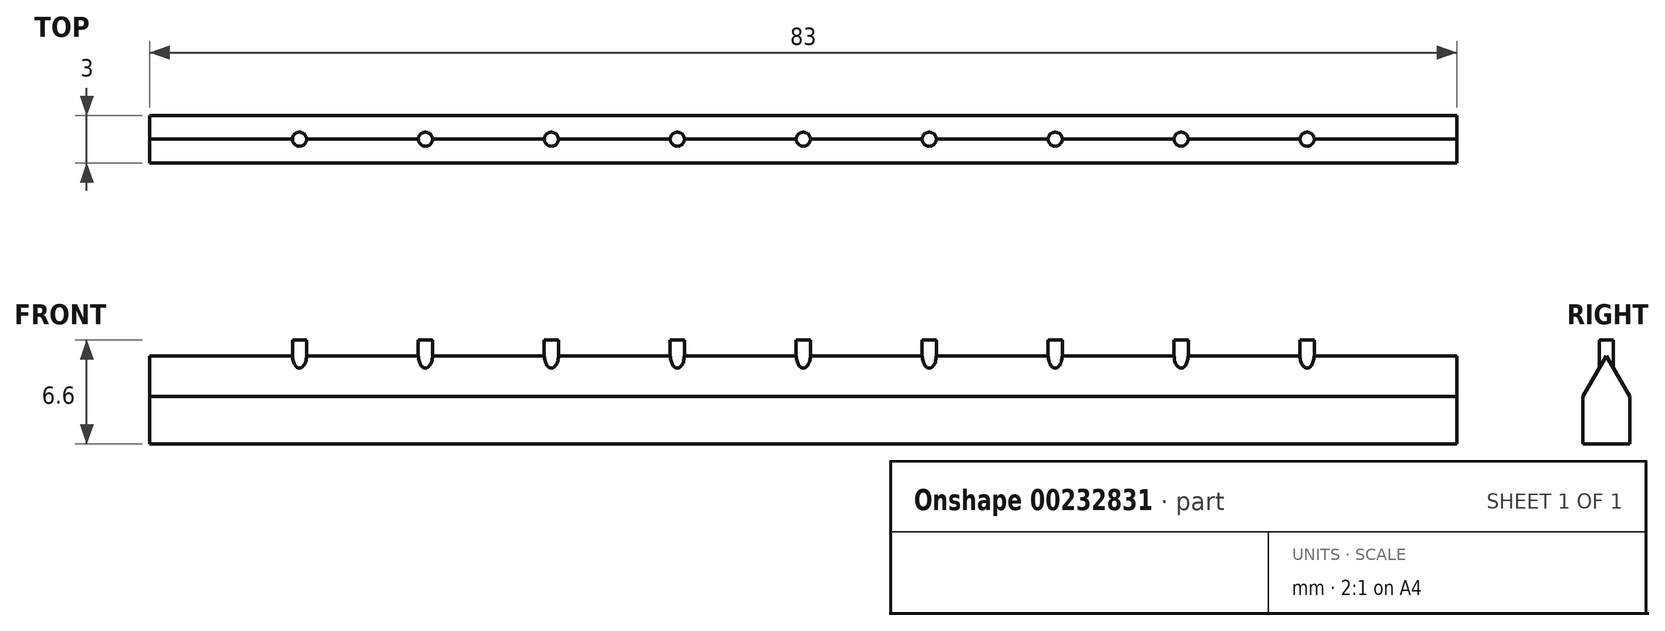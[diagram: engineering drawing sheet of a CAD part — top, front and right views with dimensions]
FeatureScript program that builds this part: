
annotation { "Feature Type Name" : "Feature", "Feature Type Description" : "" }
export const myFeature = defineFeature(function(context is Context, id is Id, definition is map)
    precondition{}
    {
        {
            var Q0;
            Q0=qCreatedBy(makeId("Right.planeOp"),FACE);
            var sketch = newSketch(context, id + "F0", { "sketchPlane" : qUnion([Q0])});
            skPoint(sketch, "E0.middle", {"position": v(0, 0) * mm});
            skLineSegment(sketch, "E1", {"start": v(-1.5, 0) * mm, "end": v(1.5, 0) * mm});
            skLineSegment(sketch, "E2", {"start": v(1.5, 0) * mm, "end": v(0, 2.6) * mm});
            skLineSegment(sketch, "E3", {"start": v(0, 2.6) * mm, "end": v(-1.5, 0) * mm});
            skSolve(sketch);
        }
        {
            var Q0;
            Q0=makeQuery(id+"F0.imprint","IMPRINT",FACE,{"disambiguationData":[TD([[makeQuery(id+"F0.imprint","IMPRINT",EDGE,{"derivedFrom":sQuery(id+"F0.wireOp",EDGE,"E1")}),1.0]])]});
            extrude(context, id + "F1", {"entities" : qUnion([Q0]), "endBound" : BoundingType.SYMMETRIC, "oppositeDirection" : true, "depth" : 83 * mm});
        }
        {
            var Q0;
            Q0=qCreatedBy(makeId("Top.planeOp"),FACE);
            var sketch = newSketch(context, id + "F2", { "sketchPlane" : qUnion([Q0])});
            skCircle(sketch, "E4", {"center": v(0, 0) * mm, "radius": 0.45 * mm});
            skCircle(sketch, "E5", {"center": v(-8, 0) * mm, "radius": 0.45 * mm});
            skCircle(sketch, "E6", {"center": v(-16, 0) * mm, "radius": 0.45 * mm});
            skCircle(sketch, "E7", {"center": v(-24, 0) * mm, "radius": 0.45 * mm});
            skCircle(sketch, "E8", {"center": v(-32, 0) * mm, "radius": 0.45 * mm});
            skCircle(sketch, "E9", {"center": v(8, 0) * mm, "radius": 0.45 * mm});
            skCircle(sketch, "E10", {"center": v(16, 0) * mm, "radius": 0.45 * mm});
            skCircle(sketch, "E11", {"center": v(24, 0) * mm, "radius": 0.45 * mm});
            skCircle(sketch, "E12", {"center": v(32, 0) * mm, "radius": 0.45 * mm});
            skSolve(sketch);
        }
        {
            var Q0;
            Q0=makeQuery(id+"F2.imprint","IMPRINT",FACE,{"disambiguationData":[TD([[makeQuery(id+"F2.imprint","IMPRINT",EDGE,{"derivedFrom":sQuery(id+"F2.wireOp",EDGE,"E8")}),1.0]])]});
            var Q1;
            Q1=makeQuery(id+"F2.imprint","IMPRINT",FACE,{"disambiguationData":[TD([[makeQuery(id+"F2.imprint","IMPRINT",EDGE,{"derivedFrom":sQuery(id+"F2.wireOp",EDGE,"E7")}),1.0]])]});
            var Q2;
            Q2=makeQuery(id+"F2.imprint","IMPRINT",FACE,{"disambiguationData":[TD([[makeQuery(id+"F2.imprint","IMPRINT",EDGE,{"derivedFrom":sQuery(id+"F2.wireOp",EDGE,"E6")}),1.0]])]});
            var Q3;
            Q3=makeQuery(id+"F2.imprint","IMPRINT",FACE,{"disambiguationData":[TD([[makeQuery(id+"F2.imprint","IMPRINT",EDGE,{"derivedFrom":sQuery(id+"F2.wireOp",EDGE,"E5")}),1.0]])]});
            var Q4;
            Q4=makeQuery(id+"F2.imprint","IMPRINT",FACE,{"disambiguationData":[TD([[makeQuery(id+"F2.imprint","IMPRINT",EDGE,{"derivedFrom":sQuery(id+"F2.wireOp",EDGE,"E4")}),1.0]])]});
            var Q5;
            Q5=makeQuery(id+"F2.imprint","IMPRINT",FACE,{"disambiguationData":[TD([[makeQuery(id+"F2.imprint","IMPRINT",EDGE,{"derivedFrom":sQuery(id+"F2.wireOp",EDGE,"E9")}),1.0]])]});
            var Q6;
            Q6=makeQuery(id+"F2.imprint","IMPRINT",FACE,{"disambiguationData":[TD([[makeQuery(id+"F2.imprint","IMPRINT",EDGE,{"derivedFrom":sQuery(id+"F2.wireOp",EDGE,"E10")}),1.0]])]});
            var Q7;
            Q7=makeQuery(id+"F2.imprint","IMPRINT",FACE,{"disambiguationData":[TD([[makeQuery(id+"F2.imprint","IMPRINT",EDGE,{"derivedFrom":sQuery(id+"F2.wireOp",EDGE,"E11")}),1.0]])]});
            var Q8;
            Q8=makeQuery(id+"F2.imprint","IMPRINT",FACE,{"disambiguationData":[TD([[makeQuery(id+"F2.imprint","IMPRINT",EDGE,{"derivedFrom":sQuery(id+"F2.wireOp",EDGE,"E12")}),1.0]])]});
            var Q9;
            Q9=sQuery(id+"F2.wireOp",EDGE,"E8");
            var Q10;
            Q10=sQuery(id+"F2.wireOp",EDGE,"E7");
            var Q11;
            Q11=sQuery(id+"F2.wireOp",EDGE,"E6");
            var Q12;
            Q12=sQuery(id+"F2.wireOp",EDGE,"E5");
            var Q13;
            Q13=sQuery(id+"F2.wireOp",EDGE,"E4");
            var Q14;
            Q14=sQuery(id+"F2.wireOp",EDGE,"E9");
            var Q15;
            Q15=sQuery(id+"F2.wireOp",EDGE,"E10");
            var Q16;
            Q16=sQuery(id+"F2.wireOp",EDGE,"E11");
            var Q17;
            Q17=sQuery(id+"F2.wireOp",EDGE,"E12");
            extrude(context, id + "F3", {"entities" : qUnion([Q0, Q1, Q2, Q3, Q4, Q5, Q6, Q7, Q8]), "operationType" : NewBodyOperationType.ADD, "surfaceEntities" : qUnion([Q9, Q10, Q11, Q12, Q13, Q14, Q15, Q16, Q17]), "depth" : 3.6 * mm});
        }
        {
            var Q0;
            Q0=makeQuery(id+"F1.opExtrude","SWEPT_FACE",FACE,{"disambiguationData":[OSD([sQuery(id+"F0.wireOp",EDGE,"E1")])]});
            extrude(context, id + "F4", {"entities" : qUnion([Q0]), "operationType" : NewBodyOperationType.ADD, "depth" : 3 * mm});
        }
    });
